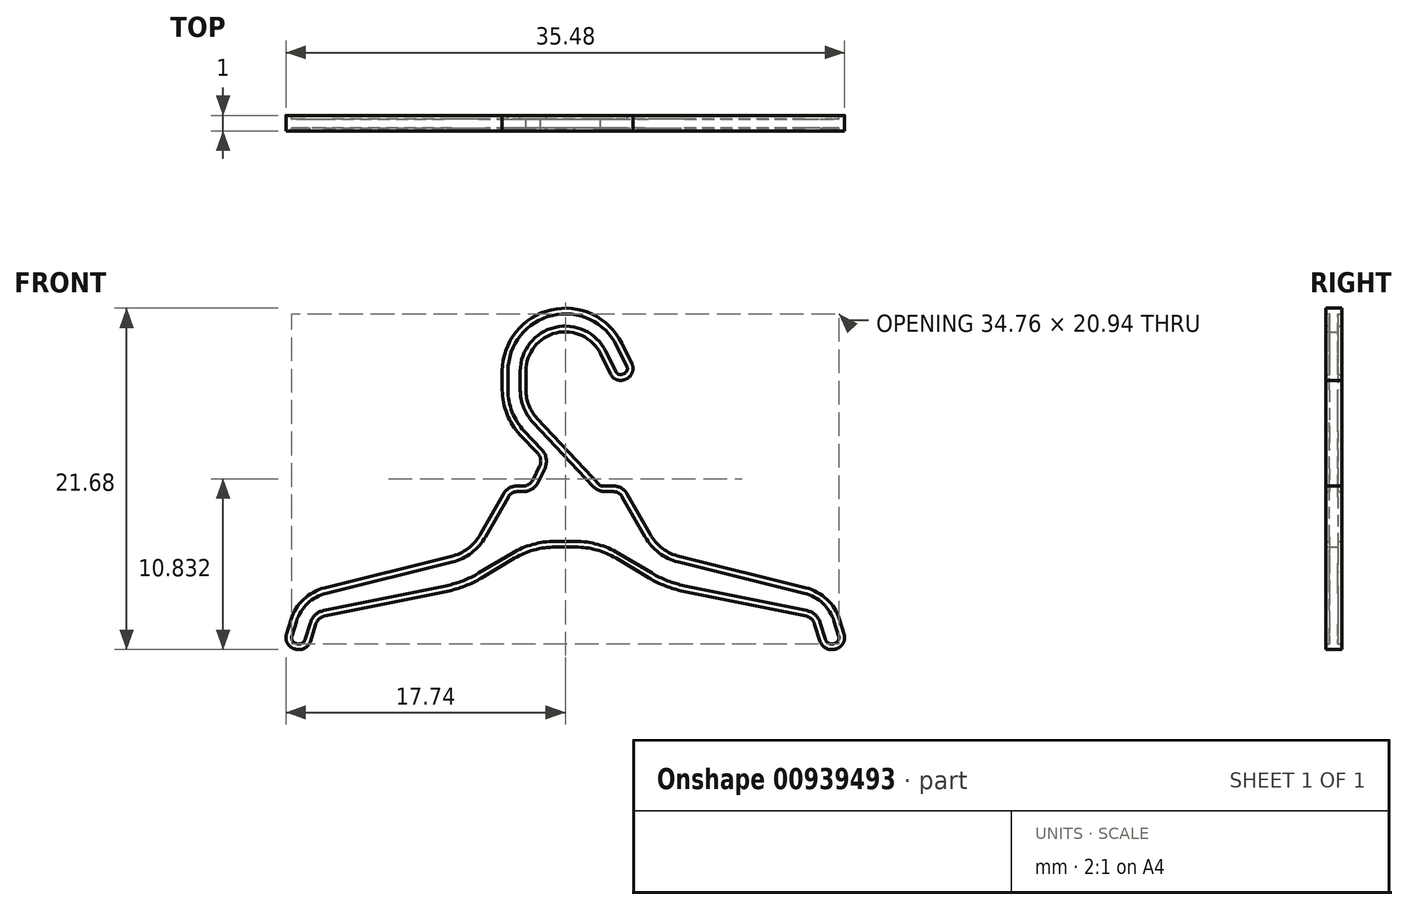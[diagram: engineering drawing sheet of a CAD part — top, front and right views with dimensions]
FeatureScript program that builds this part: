
annotation { "Feature Type Name" : "Feature", "Feature Type Description" : "" }
export const myFeature = defineFeature(function(context is Context, id is Id, definition is map)
    precondition{}
    {
        {
            var Q0;
            Q0=qCreatedBy(makeId("Front.planeOp"),FACE);
            var sketch = newSketch(context, id + "F0", { "sketchPlane" : qUnion([Q0])});
            skLineSegment(sketch, "E0", {"start": v(0, 0) * mm, "end": v(2.03, 0) * mm});
            skLineSegment(sketch, "E1", {"start": v(2.03, 0) * mm, "end": v(6.33, -2.57) * mm});
            skLineSegment(sketch, "E2", {"start": v(3.06, 3.88) * mm, "end": v(0, 3.88) * mm});
            skLineSegment(sketch, "E3", {"start": v(0, 3.88) * mm, "end": v(0, 0) * mm});
            skLineSegment(sketch, "E4", {"start": v(3.93, 3.37) * mm, "end": v(5.37, 0.83) * mm});
            skLineSegment(sketch, "E5", {"start": v(17.42, -4.6) * mm, "end": v(17.98, -6.4) * mm});
            skLineSegment(sketch, "E6", {"start": v(17.98, -6.4) * mm, "end": v(16.37, -6.57) * mm});
            skLineSegment(sketch, "E7", {"start": v(16.37, -6.57) * mm, "end": v(15.71, -4.48) * mm});
            skLineSegment(sketch, "E8", {"start": v(6.33, -2.57) * mm, "end": v(15.71, -4.48) * mm});
            skPoint(sketch, "E9.visualSharp", {"position": v(3.64, 3.88) * mm});
            skArc(sketch, "E9.filletArc", {"start": v(3.93, 3.37) * mm, "mid": v(3.56, 3.74) * mm, "end": v(3.06, 3.88) * mm});
            skLineSegment(sketch, "E10", {"start": v(7.26, -0.6) * mm, "end": v(15.28, -2.59) * mm});
            skPoint(sketch, "E11.visualSharp", {"position": v(16.92, -3) * mm});
            skArc(sketch, "E11.filletArc", {"start": v(17.42, -4.6) * mm, "mid": v(16.61, -3.32) * mm, "end": v(15.28, -2.59) * mm});
            skPoint(sketch, "E12.visualSharp", {"position": v(6.01, -0.3) * mm});
            skArc(sketch, "E12.filletArc", {"start": v(5.37, 0.83) * mm, "mid": v(6.17, -0.08) * mm, "end": v(7.26, -0.6) * mm});
            skSolve(sketch);
        }
        {
            var Q0;
            Q0=makeQuery(id+"F0.imprint","IMPRINT",FACE,{"disambiguationData":[TD([[makeQuery(id+"F0.imprint","IMPRINT",EDGE,{"derivedFrom":sQuery(id+"F0.wireOp",EDGE,"E0")}),1.0]])]});
            extrude(context, id + "F1", {"entities" : qUnion([Q0]), "depth" : 1 * mm, "offsetDistance" : 25 * mm});
        }
        {
            var Q0;
            Q0=makeQuery(id+"F1.opExtrude","SWEPT_EDGE",EDGE,{"disambiguationData":[OSD([sQuery(id+"F0.wireOp",EDGE,"E7"),sQuery(id+"F0.wireOp",EDGE,"E8")])]});
            var Q1;
            Q1=makeQuery(id+"F1.opExtrude","SWEPT_EDGE",EDGE,{"disambiguationData":[OSD([sQuery(id+"F0.wireOp",EDGE,"E6"),sQuery(id+"F0.wireOp",EDGE,"E7")])]});
            var Q2;
            Q2=makeQuery(id+"F1.opExtrude","SWEPT_EDGE",EDGE,{"disambiguationData":[OSD([sQuery(id+"F0.wireOp",EDGE,"E5"),sQuery(id+"F0.wireOp",EDGE,"E6")])]});
            fillet(context, id + "F2", {"entities" : qUnion([Q0, Q1, Q2]), "radius" : .75 * mm, "tangentPropagation" : true, "allowEdgeOverflow" : false});
        }
        {
            var Q0;
            Q0=makeQuery(id+"F1.opExtrude","SWEPT_EDGE",EDGE,{"disambiguationData":[OSD([sQuery(id+"F0.wireOp",EDGE,"E0"),sQuery(id+"F0.wireOp",EDGE,"E1")])]});
            fillet(context, id + "F3", {"entities" : qUnion([Q0]), "radius" : 5 * mm, "tangentPropagation" : true, "allowEdgeOverflow" : false});
        }
        {
            var Q0;
            Q0=makeQuery(id+"F1.opExtrude","SWEPT_EDGE",EDGE,{"disambiguationData":[OSD([sQuery(id+"F0.wireOp",EDGE,"E1"),sQuery(id+"F0.wireOp",EDGE,"E8")])]});
            fillet(context, id + "F4", {"entities" : qUnion([Q0]), "radius" : 7 * mm, "tangentPropagation" : true, "allowEdgeOverflow" : false});
        }
        {
            var Q0;
            Q0=makeQuery(id+"F1.opExtrude","SWEPT_BODY",BODY,{"disambiguationData":[OSD([sQuery(id+"F0.wireOp",EDGE,"E0"),sQuery(id+"F0.wireOp",EDGE,"E1"),sQuery(id+"F0.wireOp",EDGE,"E2"),sQuery(id+"F0.wireOp",EDGE,"E3"),sQuery(id+"F0.wireOp",EDGE,"E4"),sQuery(id+"F0.wireOp",EDGE,"E5"),sQuery(id+"F0.wireOp",EDGE,"E6"),sQuery(id+"F0.wireOp",EDGE,"E7"),sQuery(id+"F0.wireOp",EDGE,"E8"),sQuery(id+"F0.wireOp",EDGE,"E9.filletArc"),sQuery(id+"F0.wireOp",EDGE,"E10"),sQuery(id+"F0.wireOp",EDGE,"E11.filletArc"),sQuery(id+"F0.wireOp",EDGE,"E12.filletArc")])]});
            var Q1;
            Q1=makeQuery(id+"F1.opExtrude","SWEPT_FACE",FACE,{"disambiguationData":[OSD([sQuery(id+"F0.wireOp",EDGE,"E3")])]});
            mirror(context, id + "F5", {"operationType" : NewBodyOperationType.ADD, "entities" : qUnion([Q0]), "mirrorPlane" : qUnion([Q1])});
        }
        {
            var Q0;
            Q0=qCreatedBy(makeId("Front.planeOp"),FACE);
            var sketch = newSketch(context, id + "F6", { "sketchPlane" : qUnion([Q0])});
            skLineSegment(sketch, "E13", {"start": v(2.24, 3.88) * mm, "end": v(-1.78, 8.16) * mm});
            skLineSegment(sketch, "E14", {"start": v(-2.5, 9.98) * mm, "end": v(-2.5, 11.17) * mm});
            skArc(sketch, "E15", {"start": v(-2.5, 11.17) * mm, "mid": v(-0.57, 13.6) * mm, "end": v(2.24, 12.28) * mm});
            skLineSegment(sketch, "E16", {"start": v(2.24, 12.28) * mm, "end": v(3.2, 10.35) * mm});
            skLineSegment(sketch, "E17", {"start": v(-1.42, 5.58) * mm, "end": v(-2.24, 3.88) * mm});
            skLineSegment(sketch, "E18", {"start": v(-2.24, 3.88) * mm, "end": v(2.24, 3.88) * mm});
            skPoint(sketch, "E19", {"position": v(0, 3.88) * mm});
            skArc(sketch, "E20.filletArc", {"start": v(-2.5, 9.98) * mm, "mid": v(-2.31, 9) * mm, "end": v(-1.78, 8.16) * mm});
            skLineSegment(sketch, "E21.0", {"start": v(-1.42, 5.58) * mm, "end": v(-2.87, 7.13) * mm});
            skLineSegment(sketch, "E21.1", {"start": v(3.59, 12.94) * mm, "end": v(4.54, 11.01) * mm});
            skArc(sketch, "E21.2", {"start": v(-4, 11.17) * mm, "mid": v(-0.9, 15.07) * mm, "end": v(3.59, 12.94) * mm});
            skLineSegment(sketch, "E21.3", {"start": v(-4, 9.98) * mm, "end": v(-4, 11.17) * mm});
            skArc(sketch, "E21.4", {"start": v(-4, 9.98) * mm, "mid": v(-3.7, 8.45) * mm, "end": v(-2.87, 7.13) * mm});
            skLineSegment(sketch, "E22", {"start": v(3.2, 10.35) * mm, "end": v(4.54, 11.01) * mm});
            skSolve(sketch);
        }
        {
            var Q0;
            Q0=makeQuery(id+"F6.imprint","IMPRINT",FACE,{"disambiguationData":[TD([[makeQuery(id+"F6.imprint","IMPRINT",EDGE,{"derivedFrom":sQuery(id+"F6.wireOp",EDGE,"E13")}),1.0]])]});
            var Q1;
            {var subQ0=makeQuery(id+"F1.opExtrude","CAP_FACE",FACE,{"disambiguationData":[OSD([sQuery(id+"F0.wireOp",EDGE,"E0"),sQuery(id+"F0.wireOp",EDGE,"E1"),sQuery(id+"F0.wireOp",EDGE,"E2"),sQuery(id+"F0.wireOp",EDGE,"E3"),sQuery(id+"F0.wireOp",EDGE,"E4"),sQuery(id+"F0.wireOp",EDGE,"E5"),sQuery(id+"F0.wireOp",EDGE,"E6"),sQuery(id+"F0.wireOp",EDGE,"E7"),sQuery(id+"F0.wireOp",EDGE,"E8"),sQuery(id+"F0.wireOp",EDGE,"E9.filletArc"),sQuery(id+"F0.wireOp",EDGE,"E10"),sQuery(id+"F0.wireOp",EDGE,"E11.filletArc"),sQuery(id+"F0.wireOp",EDGE,"E12.filletArc")])],"isStart":false});Q1=makeQuery(id+"F5.boolean.opBoolean","MERGE",FACE,{"derivedFrom":[subQ0,makeQuery(id+"F5.opPattern","COPY",FACE,{"derivedFrom":subQ0,"instanceName":"1"})]});}
            extrude(context, id + "F7", {"entities" : qUnion([Q0]), "operationType" : NewBodyOperationType.ADD, "endBound" : BoundingType.UP_TO_SURFACE, "depth" : 25 * mm, "endBoundEntityFace" : qUnion([Q1]), "offsetDistance" : 25 * mm});
        }
        {
            var Q0;
            Q0=makeQuery(id+"F7.opExtrude","SWEPT_EDGE",EDGE,{"disambiguationData":[OSD([sQuery(id+"F6.wireOp",EDGE,"E21.1"),sQuery(id+"F6.wireOp",EDGE,"E22")])]});
            var Q1;
            Q1=makeQuery(id+"F7.opExtrude","SWEPT_EDGE",EDGE,{"disambiguationData":[OSD([sQuery(id+"F6.wireOp",EDGE,"E16"),sQuery(id+"F6.wireOp",EDGE,"E22")])]});
            var Q2;
            Q2=makeQuery(id+"F7.opExtrude","SWEPT_EDGE",EDGE,{"disambiguationData":[OSD([sQuery(id+"F6.wireOp",EDGE,"E17"),sQuery(id+"F6.wireOp",EDGE,"E21.0")])]});
            var Q3;
            Q3=makeQuery(id+"F7.opExtrude","SWEPT_EDGE",EDGE,{"disambiguationData":[OSD([sQuery(id+"F6.wireOp",EDGE,"E17"),sQuery(id+"F6.wireOp",EDGE,"E18")])]});
            var Q4;
            Q4=makeQuery(id+"F7.opExtrude","SWEPT_EDGE",EDGE,{"disambiguationData":[OSD([sQuery(id+"F6.wireOp",EDGE,"E13"),sQuery(id+"F6.wireOp",EDGE,"E18")])]});
            fillet(context, id + "F8", {"entities" : qUnion([Q0, Q1, Q2, Q3, Q4]), "radius" : .7 * mm, "tangentPropagation" : true, "allowEdgeOverflow" : false});
        }
        {
            var Q0;
            {var subQ0=makeQuery(id+"F1.opExtrude","CAP_FACE",FACE,{"disambiguationData":[OSD([sQuery(id+"F0.wireOp",EDGE,"E0"),sQuery(id+"F0.wireOp",EDGE,"E1"),sQuery(id+"F0.wireOp",EDGE,"E2"),sQuery(id+"F0.wireOp",EDGE,"E3"),sQuery(id+"F0.wireOp",EDGE,"E4"),sQuery(id+"F0.wireOp",EDGE,"E5"),sQuery(id+"F0.wireOp",EDGE,"E6"),sQuery(id+"F0.wireOp",EDGE,"E7"),sQuery(id+"F0.wireOp",EDGE,"E8"),sQuery(id+"F0.wireOp",EDGE,"E9.filletArc"),sQuery(id+"F0.wireOp",EDGE,"E10"),sQuery(id+"F0.wireOp",EDGE,"E11.filletArc"),sQuery(id+"F0.wireOp",EDGE,"E12.filletArc")])],"isStart":false});Q0=makeQuery(id+"F7.boolean.opBoolean","MERGE",FACE,{"derivedFrom":[makeQuery(id+"F5.boolean.opBoolean","MERGE",FACE,{"derivedFrom":[subQ0,makeQuery(id+"F5.opPattern","COPY",FACE,{"derivedFrom":subQ0,"instanceName":"1"})]}),makeQuery(id+"F7.opExtrude","CAP_FACE",FACE,{"disambiguationData":[OSD([sQuery(id+"F6.wireOp",EDGE,"E13"),sQuery(id+"F6.wireOp",EDGE,"E14"),sQuery(id+"F6.wireOp",EDGE,"E15"),sQuery(id+"F6.wireOp",EDGE,"E16"),sQuery(id+"F6.wireOp",EDGE,"E17"),sQuery(id+"F6.wireOp",EDGE,"E18"),sQuery(id+"F6.wireOp",EDGE,"E20.filletArc"),sQuery(id+"F6.wireOp",EDGE,"E21.0"),sQuery(id+"F6.wireOp",EDGE,"E21.1"),sQuery(id+"F6.wireOp",EDGE,"E21.2"),sQuery(id+"F6.wireOp",EDGE,"E21.3"),sQuery(id+"F6.wireOp",EDGE,"E21.4"),sQuery(id+"F6.wireOp",EDGE,"E22")])],"isStart":false})]});}
            var sketch = newSketch(context, id + "F9", { "sketchPlane" : qUnion([Q0])});
            skLineSegment(sketch, "E23.0", {"start": v(2.57, 12.44) * mm, "end": v(3.2, 11.14) * mm});
            skArc(sketch, "E23.1", {"start": v(-2.86, 11.17) * mm, "mid": v(-0.65, 13.96) * mm, "end": v(2.57, 12.44) * mm});
            skLineSegment(sketch, "E23.2", {"start": v(-2.86, 9.98) * mm, "end": v(-2.86, 11.17) * mm});
            skArc(sketch, "E23.3", {"start": v(-2.04, 7.91) * mm, "mid": v(-2.65, 8.87) * mm, "end": v(-2.86, 9.98) * mm});
            skLineSegment(sketch, "E23.4", {"start": v(-16.53, -5.88) * mm, "end": v(-16.19, -4.8) * mm});
            skArc(sketch, "E23.5", {"start": v(-16.94, -6.15) * mm, "mid": v(-16.68, -6.09) * mm, "end": v(-16.53, -5.88) * mm});
            skLineSegment(sketch, "E23.6", {"start": v(-17.03, -6.14) * mm, "end": v(-16.94, -6.15) * mm});
            skArc(sketch, "E23.7", {"start": v(-17.36, -5.63) * mm, "mid": v(-17.32, -5.96) * mm, "end": v(-17.03, -6.14) * mm});
            skLineSegment(sketch, "E23.8", {"start": v(-17.08, -4.71) * mm, "end": v(-17.36, -5.63) * mm});
            skArc(sketch, "E23.9", {"start": v(-15.2, -2.94) * mm, "mid": v(-16.37, -3.58) * mm, "end": v(-17.08, -4.71) * mm});
            skLineSegment(sketch, "E23.10", {"start": v(-7.17, -0.95) * mm, "end": v(-15.2, -2.94) * mm});
            skArc(sketch, "E23.11", {"start": v(-5.06, 0.65) * mm, "mid": v(-5.95, -0.37) * mm, "end": v(-7.17, -0.95) * mm});
            skLineSegment(sketch, "E23.12", {"start": v(-3.61, 3.2) * mm, "end": v(-5.06, 0.65) * mm});
            skArc(sketch, "E23.13", {"start": v(-3.06, 3.52) * mm, "mid": v(-3.38, 3.43) * mm, "end": v(-3.61, 3.2) * mm});
            skLineSegment(sketch, "E23.14", {"start": v(-2.68, 3.52) * mm, "end": v(-3.06, 3.52) * mm});
            skArc(sketch, "E23.15", {"start": v(-1.73, 4.12) * mm, "mid": v(-2.12, 3.68) * mm, "end": v(-2.68, 3.52) * mm});
            skLineSegment(sketch, "E23.16", {"start": v(3.9, 11.48) * mm, "end": v(3.26, 12.78) * mm});
            skArc(sketch, "E23.17", {"start": v(3.75, 11.03) * mm, "mid": v(3.92, 11.22) * mm, "end": v(3.9, 11.48) * mm});
            skLineSegment(sketch, "E23.18", {"start": v(3.66, 10.98) * mm, "end": v(3.75, 11.03) * mm});
            skArc(sketch, "E23.19", {"start": v(3.2, 11.14) * mm, "mid": v(3.4, 10.96) * mm, "end": v(3.66, 10.98) * mm});
            skArc(sketch, "E23.20", {"start": v(-3.64, 11.17) * mm, "mid": v(-0.83, 14.72) * mm, "end": v(3.26, 12.78) * mm});
            skLineSegment(sketch, "E23.21", {"start": v(-3.64, 11.17) * mm, "end": v(-3.64, 9.98) * mm});
            skArc(sketch, "E23.22", {"start": v(-3.64, 9.98) * mm, "mid": v(-3.37, 8.58) * mm, "end": v(-2.61, 7.38) * mm});
            skLineSegment(sketch, "E23.23", {"start": v(-2.61, 7.38) * mm, "end": v(-1.48, 6.18) * mm});
            skArc(sketch, "E23.24", {"start": v(-1.48, 6.18) * mm, "mid": v(-1.2, 5.61) * mm, "end": v(-1.3, 4.99) * mm});
            skLineSegment(sketch, "E23.25", {"start": v(-1.3, 4.99) * mm, "end": v(-1.73, 4.12) * mm});
            skArc(sketch, "E23.26", {"start": v(-15.35, -4.04) * mm, "mid": v(-15.87, -4.3) * mm, "end": v(-16.19, -4.8) * mm});
            skLineSegment(sketch, "E23.27", {"start": v(-15.35, -4.04) * mm, "end": v(-7.58, -2.46) * mm});
            skArc(sketch, "E23.28", {"start": v(-7.58, -2.46) * mm, "mid": v(-6.5, -2.14) * mm, "end": v(-5.5, -1.65) * mm});
            skLineSegment(sketch, "E23.29", {"start": v(-5.5, -1.65) * mm, "end": v(-3.4, -0.4) * mm});
            skArc(sketch, "E23.30", {"start": v(-0.65, 0.36) * mm, "mid": v(-2.07, 0.17) * mm, "end": v(-3.4, -0.4) * mm});
            skLineSegment(sketch, "E23.31", {"start": v(-0.65, 0.36) * mm, "end": v(0.65, 0.36) * mm});
            skArc(sketch, "E23.32", {"start": v(0.65, 0.36) * mm, "mid": v(2.07, 0.17) * mm, "end": v(3.4, -0.4) * mm});
            skLineSegment(sketch, "E23.33", {"start": v(3.4, -0.4) * mm, "end": v(5.5, -1.65) * mm});
            skArc(sketch, "E23.34", {"start": v(5.5, -1.65) * mm, "mid": v(6.5, -2.14) * mm, "end": v(7.58, -2.46) * mm});
            skLineSegment(sketch, "E23.35", {"start": v(7.58, -2.46) * mm, "end": v(15.35, -4.04) * mm});
            skArc(sketch, "E23.36", {"start": v(15.35, -4.04) * mm, "mid": v(15.87, -4.3) * mm, "end": v(16.19, -4.8) * mm});
            skLineSegment(sketch, "E23.37", {"start": v(16.19, -4.8) * mm, "end": v(16.53, -5.88) * mm});
            skArc(sketch, "E23.38", {"start": v(16.53, -5.88) * mm, "mid": v(16.68, -6.09) * mm, "end": v(16.94, -6.15) * mm});
            skLineSegment(sketch, "E23.39", {"start": v(16.94, -6.15) * mm, "end": v(17.03, -6.14) * mm});
            skArc(sketch, "E23.40", {"start": v(17.03, -6.14) * mm, "mid": v(17.32, -5.96) * mm, "end": v(17.36, -5.63) * mm});
            skLineSegment(sketch, "E23.41", {"start": v(17.36, -5.63) * mm, "end": v(17.08, -4.71) * mm});
            skArc(sketch, "E23.42", {"start": v(17.08, -4.71) * mm, "mid": v(16.37, -3.58) * mm, "end": v(15.2, -2.94) * mm});
            skLineSegment(sketch, "E23.43", {"start": v(15.2, -2.94) * mm, "end": v(7.17, -0.95) * mm});
            skArc(sketch, "E23.44", {"start": v(7.17, -0.95) * mm, "mid": v(5.95, -0.37) * mm, "end": v(5.06, 0.65) * mm});
            skLineSegment(sketch, "E23.45", {"start": v(5.06, 0.65) * mm, "end": v(3.61, 3.2) * mm});
            skArc(sketch, "E23.46", {"start": v(3.61, 3.2) * mm, "mid": v(3.38, 3.43) * mm, "end": v(3.06, 3.52) * mm});
            skLineSegment(sketch, "E23.47", {"start": v(3.06, 3.52) * mm, "end": v(2.54, 3.52) * mm});
            skArc(sketch, "E23.48", {"start": v(2.54, 3.52) * mm, "mid": v(2.12, 3.6) * mm, "end": v(1.77, 3.85) * mm});
            skLineSegment(sketch, "E23.49", {"start": v(1.77, 3.85) * mm, "end": v(-2.04, 7.91) * mm});
            skSolve(sketch);
        }
        {
            var Q0;
            {var subQ0=makeQuery(id+"F1.opExtrude","CAP_FACE",FACE,{"disambiguationData":[OSD([sQuery(id+"F0.wireOp",EDGE,"E0"),sQuery(id+"F0.wireOp",EDGE,"E1"),sQuery(id+"F0.wireOp",EDGE,"E2"),sQuery(id+"F0.wireOp",EDGE,"E3"),sQuery(id+"F0.wireOp",EDGE,"E4"),sQuery(id+"F0.wireOp",EDGE,"E5"),sQuery(id+"F0.wireOp",EDGE,"E6"),sQuery(id+"F0.wireOp",EDGE,"E7"),sQuery(id+"F0.wireOp",EDGE,"E8"),sQuery(id+"F0.wireOp",EDGE,"E9.filletArc"),sQuery(id+"F0.wireOp",EDGE,"E10"),sQuery(id+"F0.wireOp",EDGE,"E11.filletArc"),sQuery(id+"F0.wireOp",EDGE,"E12.filletArc")])],"isStart":true});Q0=makeQuery(id+"F7.boolean.opBoolean","MERGE",FACE,{"derivedFrom":[makeQuery(id+"F5.boolean.opBoolean","MERGE",FACE,{"derivedFrom":[subQ0,makeQuery(id+"F5.opPattern","COPY",FACE,{"derivedFrom":subQ0,"instanceName":"1"})]}),makeQuery(id+"F7.opExtrude","CAP_FACE",FACE,{"disambiguationData":[OSD([sQuery(id+"F6.wireOp",EDGE,"E13"),sQuery(id+"F6.wireOp",EDGE,"E14"),sQuery(id+"F6.wireOp",EDGE,"E15"),sQuery(id+"F6.wireOp",EDGE,"E16"),sQuery(id+"F6.wireOp",EDGE,"E17"),sQuery(id+"F6.wireOp",EDGE,"E18"),sQuery(id+"F6.wireOp",EDGE,"E20.filletArc"),sQuery(id+"F6.wireOp",EDGE,"E21.0"),sQuery(id+"F6.wireOp",EDGE,"E21.1"),sQuery(id+"F6.wireOp",EDGE,"E21.2"),sQuery(id+"F6.wireOp",EDGE,"E21.3"),sQuery(id+"F6.wireOp",EDGE,"E21.4"),sQuery(id+"F6.wireOp",EDGE,"E22")])],"isStart":true})]});}
            var sketch = newSketch(context, id + "F10", { "sketchPlane" : qUnion([Q0])});
            skLineSegment(sketch, "E24.0", {"start": v(-2.57, 12.44) * mm, "end": v(-3.2, 11.14) * mm});
            skArc(sketch, "E24.1", {"start": v(2.86, 11.17) * mm, "mid": v(0.65, 13.96) * mm, "end": v(-2.57, 12.44) * mm});
            skLineSegment(sketch, "E24.2", {"start": v(2.86, 9.98) * mm, "end": v(2.86, 11.17) * mm});
            skArc(sketch, "E24.3", {"start": v(2.04, 7.91) * mm, "mid": v(2.65, 8.87) * mm, "end": v(2.86, 9.98) * mm});
            skLineSegment(sketch, "E24.4", {"start": v(16.53, -5.88) * mm, "end": v(16.19, -4.8) * mm});
            skArc(sketch, "E24.5", {"start": v(16.94, -6.15) * mm, "mid": v(16.68, -6.09) * mm, "end": v(16.53, -5.88) * mm});
            skLineSegment(sketch, "E24.6", {"start": v(17.03, -6.14) * mm, "end": v(16.94, -6.15) * mm});
            skArc(sketch, "E24.7", {"start": v(17.36, -5.63) * mm, "mid": v(17.32, -5.96) * mm, "end": v(17.03, -6.14) * mm});
            skLineSegment(sketch, "E24.8", {"start": v(17.08, -4.71) * mm, "end": v(17.36, -5.63) * mm});
            skArc(sketch, "E24.9", {"start": v(15.2, -2.94) * mm, "mid": v(16.37, -3.58) * mm, "end": v(17.08, -4.71) * mm});
            skLineSegment(sketch, "E24.10", {"start": v(7.17, -0.95) * mm, "end": v(15.2, -2.94) * mm});
            skArc(sketch, "E24.11", {"start": v(5.06, 0.65) * mm, "mid": v(5.95, -0.37) * mm, "end": v(7.17, -0.95) * mm});
            skLineSegment(sketch, "E24.12", {"start": v(3.61, 3.2) * mm, "end": v(5.06, 0.65) * mm});
            skArc(sketch, "E24.13", {"start": v(3.06, 3.52) * mm, "mid": v(3.38, 3.43) * mm, "end": v(3.61, 3.2) * mm});
            skLineSegment(sketch, "E24.14", {"start": v(2.68, 3.52) * mm, "end": v(3.06, 3.52) * mm});
            skArc(sketch, "E24.15", {"start": v(1.73, 4.12) * mm, "mid": v(2.12, 3.68) * mm, "end": v(2.68, 3.52) * mm});
            skLineSegment(sketch, "E24.16", {"start": v(-3.9, 11.48) * mm, "end": v(-3.26, 12.78) * mm});
            skArc(sketch, "E24.17", {"start": v(-3.75, 11.03) * mm, "mid": v(-3.92, 11.22) * mm, "end": v(-3.9, 11.48) * mm});
            skLineSegment(sketch, "E24.18", {"start": v(-3.66, 10.98) * mm, "end": v(-3.75, 11.03) * mm});
            skArc(sketch, "E24.19", {"start": v(-3.2, 11.14) * mm, "mid": v(-3.4, 10.96) * mm, "end": v(-3.66, 10.98) * mm});
            skArc(sketch, "E24.20", {"start": v(3.64, 11.17) * mm, "mid": v(0.83, 14.72) * mm, "end": v(-3.26, 12.78) * mm});
            skLineSegment(sketch, "E24.21", {"start": v(3.64, 11.17) * mm, "end": v(3.64, 9.98) * mm});
            skArc(sketch, "E24.22", {"start": v(3.64, 9.98) * mm, "mid": v(3.37, 8.58) * mm, "end": v(2.61, 7.38) * mm});
            skLineSegment(sketch, "E24.23", {"start": v(2.61, 7.38) * mm, "end": v(1.48, 6.18) * mm});
            skArc(sketch, "E24.24", {"start": v(1.48, 6.18) * mm, "mid": v(1.2, 5.61) * mm, "end": v(1.3, 4.99) * mm});
            skLineSegment(sketch, "E24.25", {"start": v(1.3, 4.99) * mm, "end": v(1.73, 4.12) * mm});
            skArc(sketch, "E24.26", {"start": v(15.35, -4.04) * mm, "mid": v(15.87, -4.3) * mm, "end": v(16.19, -4.8) * mm});
            skLineSegment(sketch, "E24.27", {"start": v(15.35, -4.04) * mm, "end": v(7.58, -2.46) * mm});
            skArc(sketch, "E24.28", {"start": v(7.58, -2.46) * mm, "mid": v(6.5, -2.14) * mm, "end": v(5.5, -1.65) * mm});
            skLineSegment(sketch, "E24.29", {"start": v(5.5, -1.65) * mm, "end": v(3.4, -0.4) * mm});
            skArc(sketch, "E24.30", {"start": v(0.65, 0.36) * mm, "mid": v(2.07, 0.17) * mm, "end": v(3.4, -0.4) * mm});
            skLineSegment(sketch, "E24.31", {"start": v(0.65, 0.36) * mm, "end": v(-0.65, 0.36) * mm});
            skArc(sketch, "E24.32", {"start": v(-0.65, 0.36) * mm, "mid": v(-2.07, 0.17) * mm, "end": v(-3.4, -0.4) * mm});
            skLineSegment(sketch, "E24.33", {"start": v(-3.4, -0.4) * mm, "end": v(-5.5, -1.65) * mm});
            skArc(sketch, "E24.34", {"start": v(-5.5, -1.65) * mm, "mid": v(-6.5, -2.14) * mm, "end": v(-7.58, -2.46) * mm});
            skLineSegment(sketch, "E24.35", {"start": v(-7.58, -2.46) * mm, "end": v(-15.35, -4.04) * mm});
            skArc(sketch, "E24.36", {"start": v(-15.35, -4.04) * mm, "mid": v(-15.87, -4.3) * mm, "end": v(-16.19, -4.8) * mm});
            skLineSegment(sketch, "E24.37", {"start": v(-16.19, -4.8) * mm, "end": v(-16.53, -5.88) * mm});
            skArc(sketch, "E24.38", {"start": v(-16.53, -5.88) * mm, "mid": v(-16.68, -6.09) * mm, "end": v(-16.94, -6.15) * mm});
            skLineSegment(sketch, "E24.39", {"start": v(-16.94, -6.15) * mm, "end": v(-17.03, -6.14) * mm});
            skArc(sketch, "E24.40", {"start": v(-17.03, -6.14) * mm, "mid": v(-17.32, -5.96) * mm, "end": v(-17.36, -5.63) * mm});
            skLineSegment(sketch, "E24.41", {"start": v(-17.36, -5.63) * mm, "end": v(-17.08, -4.71) * mm});
            skArc(sketch, "E24.42", {"start": v(-17.08, -4.71) * mm, "mid": v(-16.37, -3.58) * mm, "end": v(-15.2, -2.94) * mm});
            skLineSegment(sketch, "E24.43", {"start": v(-15.2, -2.94) * mm, "end": v(-7.17, -0.95) * mm});
            skArc(sketch, "E24.44", {"start": v(-7.17, -0.95) * mm, "mid": v(-5.95, -0.37) * mm, "end": v(-5.06, 0.65) * mm});
            skLineSegment(sketch, "E24.45", {"start": v(-5.06, 0.65) * mm, "end": v(-3.61, 3.2) * mm});
            skArc(sketch, "E24.46", {"start": v(-3.61, 3.2) * mm, "mid": v(-3.38, 3.43) * mm, "end": v(-3.06, 3.52) * mm});
            skLineSegment(sketch, "E24.47", {"start": v(-3.06, 3.52) * mm, "end": v(-2.54, 3.52) * mm});
            skArc(sketch, "E24.48", {"start": v(-2.54, 3.52) * mm, "mid": v(-2.12, 3.6) * mm, "end": v(-1.77, 3.85) * mm});
            skLineSegment(sketch, "E24.49", {"start": v(-1.77, 3.85) * mm, "end": v(2.04, 7.91) * mm});
            skSolve(sketch);
        }
        {
            var Q0;
            Q0=makeQuery(id+"F9.imprint","IMPRINT",FACE,{"disambiguationData":[TD([[makeQuery(id+"F9.imprint","IMPRINT",EDGE,{"derivedFrom":sQuery(id+"F9.wireOp",EDGE,"E23.0")}),1.0]])]});
            extrude(context, id + "F11", {"entities" : qUnion([Q0]), "operationType" : NewBodyOperationType.REMOVE, "oppositeDirection" : true, "depth" : .2 * mm, "offsetDistance" : 25 * mm, "hasDraft" : true, "draftAngle" : 3 * degree});
        }
        {
            var Q0;
            Q0=makeQuery(id+"F10.imprint","IMPRINT",FACE,{"disambiguationData":[TD([[makeQuery(id+"F10.imprint","IMPRINT",EDGE,{"derivedFrom":sQuery(id+"F10.wireOp",EDGE,"E24.0")}),-1.0]])]});
            extrude(context, id + "F12", {"entities" : qUnion([Q0]), "operationType" : NewBodyOperationType.REMOVE, "oppositeDirection" : true, "depth" : .25 * mm, "offsetDistance" : 25 * mm});
        }
    });
